# Revit family: Electrical-Box_FSR_OWB-X3_FlushMount
name_source: partatom
category: Electrical Fixtures
units: mm (PartAtom-declared; Revit-internal decimal feet)

## family parameters
Always vertical = Yes
Classification Number = 23.85.10.17.11
Cut with Voids When Loaded = No
Host = Wall
Maintain Annotation Orientation = No
Part Type = Normal
Room Calculation Point = No
Round Connector Dimension = Use Diameter
Shared = No

## types (5) — shared parameters
Assembly Code = D5020100
Body Material = Material and Finish as Specified in 26 27 26
Building Codes = ftp://doclib.fsrinc.com/
Construction Details = ftp://doclib.fsrinc.com/
Cover Material = Material and Finish as Specified in 26 27 26
Default Elevation = 0"
Description = Electrical Box as Specified in 26 27 26
Glazing = Translucent Plastic
Green Building-LEED = http://www.arcat.com
Gross Depth = 5 53/64"
Gross Height = 20"
Gross Projection = 1 171/256"
Gross Width = 15"
Installation-Fabrication = ftp://doclib.fsrinc.com/
Keynote = 26 27 26
Manufacturer = FSR Inc.
Manufacturer Fax = 973-785-4207
Manufacturer Website = http://www.fsrinc.com
Model = As Specified in 26 27 26
Product Data = http://www.arcat.com
Sales Information = http://www.fsrinc.com
Specification = http://www.arcat.com
Test Data = ftp://doclib.fsrinc.com/
Trim Material = Material and Finish as Specified in 26 27 26
URL = http://www.fsrinc.com
zero-valued in all types: Expected Lifespan (Years), Maintenance Schedule (Months), Warranty Duration (Years)

## per-type parameters (varying)
| type | Internal Plate Type |
| OWB-X3-FM-PLT | Internal Plate : Blank Plate |
| OWB-X3-FM-XLR | Internal Plate : (32) XLR Holes |
| OWB-X3-FM-IPS | Internal Plate : (36) IPS Slots |
| OWB-X3-FM-GNG | Internal Plate : (3) 2 Gang & (1) 4 Gang Openings |
| OWB-X3-FM | Internal Plate : None |

## geometry (parser evidence)
native form markers: Sweep x9
no freeform markers — native parametric forms only
